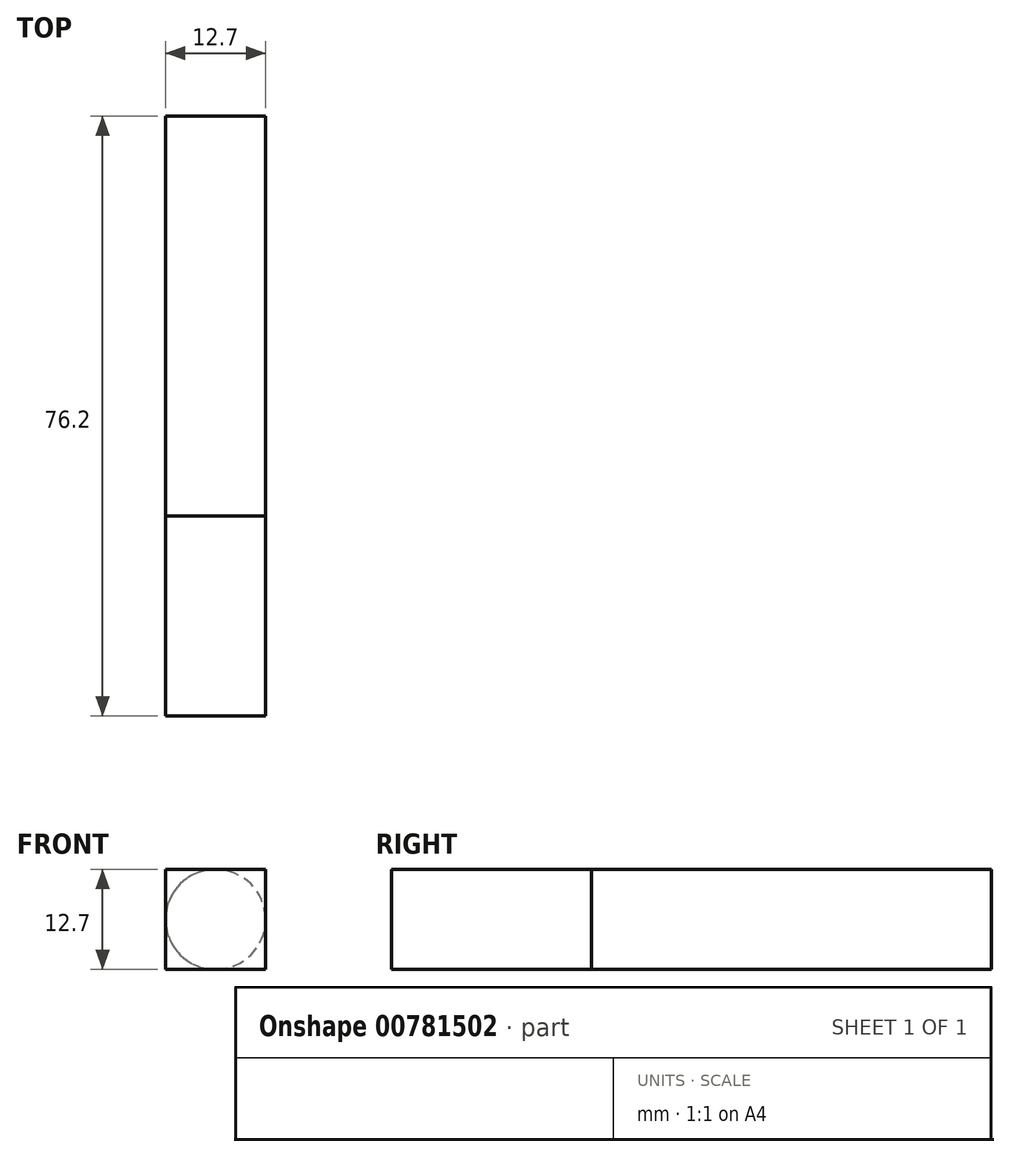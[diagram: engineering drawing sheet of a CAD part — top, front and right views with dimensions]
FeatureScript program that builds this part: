
annotation { "Feature Type Name" : "Feature", "Feature Type Description" : "" }
export const myFeature = defineFeature(function(context is Context, id is Id, definition is map)
    precondition{}
    {
        {
            var Q0;
            Q0=qCreatedBy(makeId("Front.planeOp"),FACE);
            var sketch = newSketch(context, id + "F0", { "sketchPlane" : qUnion([Q0])});
            skCircle(sketch, "E0", {"center": v(0, 0) * mm, "radius": 6.35 * mm});
            skSolve(sketch);
        }
        {
            var Q0;
            Q0 = qSketchRegion(id + "F0", true);
            extrude(context, id + "F1", {"entities" : qUnion([Q0]), "depth" : 50.8 * mm, "offsetDistance" : 25.4 * mm});
        }
        {
            var Q0;
            Q0=makeQuery(id+"F1.opExtrude","CAP_FACE",FACE,{"disambiguationData":[OSD([sQuery(id+"F0.wireOp",EDGE,"E0")])],"isStart":false});
            var sketch = newSketch(context, id + "F2", { "sketchPlane" : qUnion([Q0])});
            skLineSegment(sketch, "E1.bottom", {"start": v(6.35, 6.35) * mm, "end": v(-6.35, 6.35) * mm});
            skLineSegment(sketch, "E1.top", {"start": v(6.35, -6.35) * mm, "end": v(-6.35, -6.35) * mm});
            skLineSegment(sketch, "E1.left", {"start": v(6.35, 6.35) * mm, "end": v(6.35, -6.35) * mm});
            skLineSegment(sketch, "E1.right", {"start": v(-6.35, 6.35) * mm, "end": v(-6.35, -6.35) * mm});
            skPoint(sketch, "E1.middle", {"position": v(0, 0) * mm});
            skSolve(sketch);
        }
        {
            var Q0;
            Q0 = qSketchRegion(id + "F2", true);
            extrude(context, id + "F3", {"entities" : qUnion([Q0]), "operationType" : NewBodyOperationType.ADD, "depth" : 25.4 * mm, "offsetDistance" : 25.4 * mm});
        }
    });
